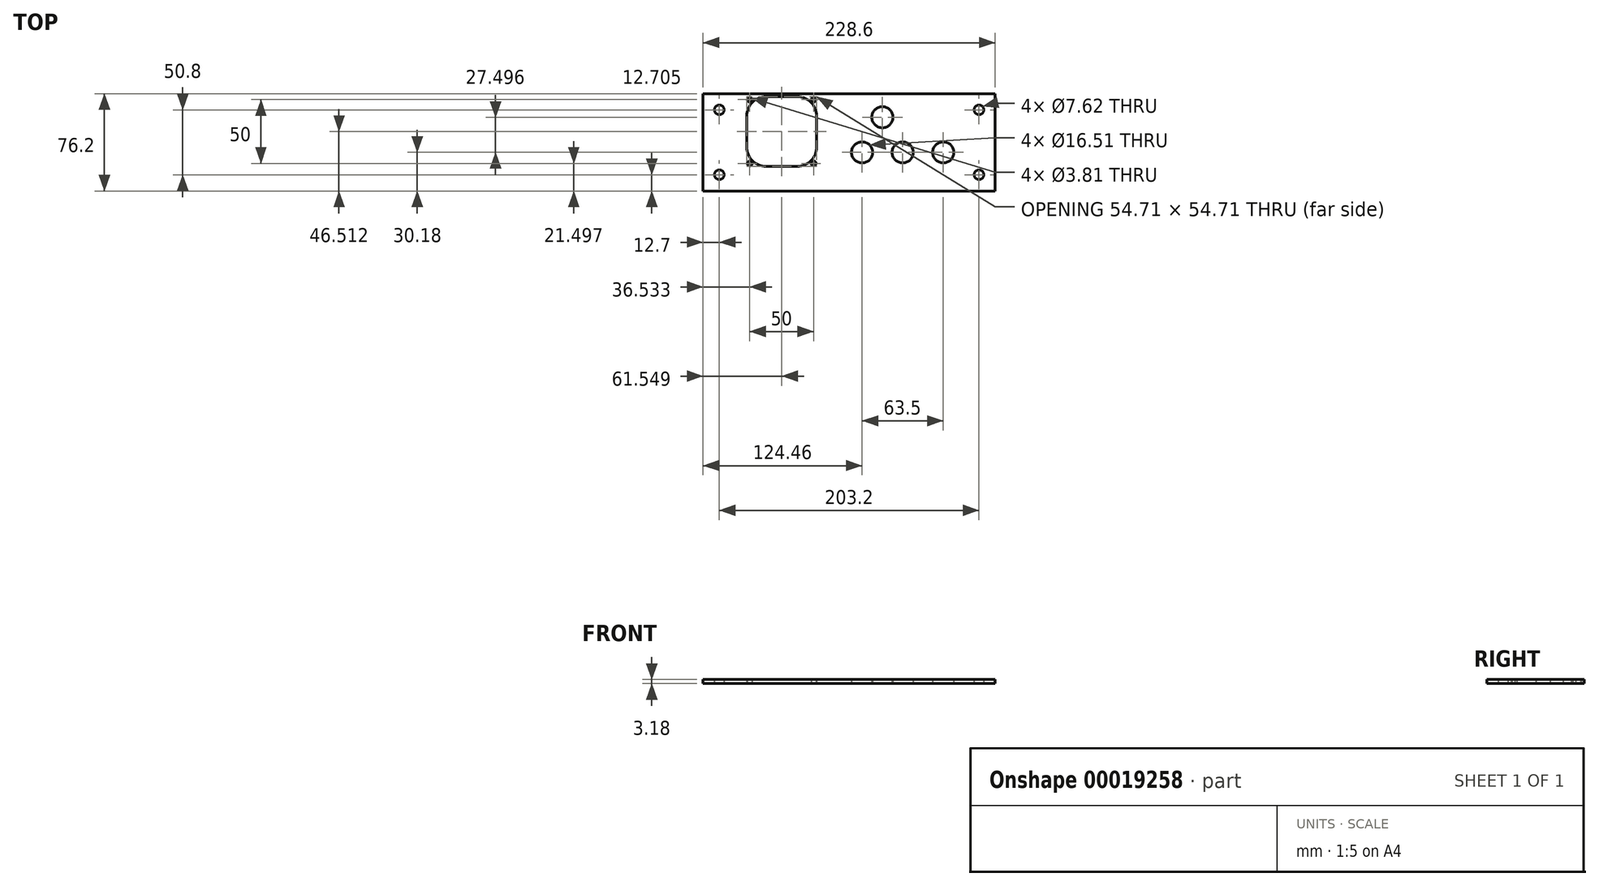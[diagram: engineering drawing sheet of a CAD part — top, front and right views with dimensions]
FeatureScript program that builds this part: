
annotation { "Feature Type Name" : "Feature", "Feature Type Description" : "" }
export const myFeature = defineFeature(function(context is Context, id is Id, definition is map)
    precondition{}
    {
        {
            var Q0;
            Q0=qCreatedBy(makeId("Top.planeOp"),FACE);
            var sketch = newSketch(context, id + "F0", { "sketchPlane" : qUnion([Q0])});
            skLineSegment(sketch, "E0.bottom", {"start": v(-121.64, 45.12) * mm, "end": v(106.96, 45.12) * mm});
            skLineSegment(sketch, "E0.top", {"start": v(-121.64, -31.08) * mm, "end": v(106.96, -31.08) * mm});
            skLineSegment(sketch, "E0.left", {"start": v(-121.64, 45.12) * mm, "end": v(-121.64, -31.08) * mm});
            skLineSegment(sketch, "E0.right", {"start": v(106.96, 45.12) * mm, "end": v(106.96, -31.08) * mm});
            skLineSegment(sketch, "E1", {"start": v(-96.24, 45.12) * mm, "end": v(-96.24, -31.08) * mm, "construction": true});
            skLineSegment(sketch, "E2", {"start": v(81.56, 45.12) * mm, "end": v(81.56, -31.08) * mm, "construction": true});
            skLineSegment(sketch, "E3", {"start": v(-121.64, 19.72) * mm, "end": v(-96.24, 19.72) * mm, "construction": true});
            skLineSegment(sketch, "E4", {"start": v(-121.64, -5.68) * mm, "end": v(-96.24, -5.68) * mm, "construction": true});
            skLineSegment(sketch, "E5", {"start": v(81.56, 19.72) * mm, "end": v(106.96, 19.72) * mm, "construction": true});
            skLineSegment(sketch, "E6", {"start": v(81.56, -5.68) * mm, "end": v(106.96, -5.68) * mm, "construction": true});
            skLineSegment(sketch, "E7", {"start": v(-96.24, 45.12) * mm, "end": v(-121.64, 19.72) * mm, "construction": true});
            skLineSegment(sketch, "E8", {"start": v(81.56, 45.12) * mm, "end": v(106.96, 19.72) * mm, "construction": true});
            skLineSegment(sketch, "E9", {"start": v(81.56, -31.08) * mm, "end": v(106.96, -5.68) * mm, "construction": true});
            skLineSegment(sketch, "E10", {"start": v(-96.24, -31.08) * mm, "end": v(-121.64, -5.68) * mm, "construction": true});
            skCircle(sketch, "E11", {"center": v(-108.94, 32.42) * mm, "radius": 3.81 * mm});
            skCircle(sketch, "E12", {"center": v(-108.94, -18.38) * mm, "radius": 3.81 * mm});
            skCircle(sketch, "E13", {"center": v(94.26, 32.42) * mm, "radius": 3.81 * mm});
            skCircle(sketch, "E14", {"center": v(94.26, -18.38) * mm, "radius": 3.81 * mm});
            skCircle(sketch, "E15", {"center": v(66.32, -0.9) * mm, "radius": 8.26 * mm});
            skCircle(sketch, "E16", {"center": v(34.57, -0.9) * mm, "radius": 8.26 * mm});
            skCircle(sketch, "E17", {"center": v(2.82, -0.9) * mm, "radius": 8.26 * mm});
            skLineSegment(sketch, "E18.bottom", {"start": v(-72.2, 42.79) * mm, "end": v(-47.98, 42.79) * mm});
            skLineSegment(sketch, "E18.top", {"start": v(-72.2, -11.92) * mm, "end": v(-47.98, -11.92) * mm});
            skLineSegment(sketch, "E18.left", {"start": v(-87.45, 27.55) * mm, "end": v(-87.45, 3.32) * mm});
            skLineSegment(sketch, "E18.right", {"start": v(-32.74, 27.55) * mm, "end": v(-32.74, 3.32) * mm});
            skPoint(sketch, "E19.visualSharp", {"position": v(-87.45, 42.79) * mm});
            skArc(sketch, "E19.filletArc", {"start": v(-72.2, 42.79) * mm, "mid": v(-82.98, 38.32) * mm, "end": v(-87.45, 27.55) * mm});
            skPoint(sketch, "E20.visualSharp", {"position": v(-32.74, 42.79) * mm});
            skArc(sketch, "E20.filletArc", {"start": v(-32.74, 27.55) * mm, "mid": v(-37.2, 38.32) * mm, "end": v(-47.98, 42.79) * mm});
            skPoint(sketch, "E21.visualSharp", {"position": v(-32.74, -11.92) * mm});
            skArc(sketch, "E21.filletArc", {"start": v(-47.98, -11.92) * mm, "mid": v(-37.2, -7.46) * mm, "end": v(-32.74, 3.32) * mm});
            skPoint(sketch, "E22.visualSharp", {"position": v(-87.45, -11.92) * mm});
            skArc(sketch, "E22.filletArc", {"start": v(-87.45, 3.32) * mm, "mid": v(-82.98, -7.46) * mm, "end": v(-72.2, -11.92) * mm});
            skLineSegment(sketch, "E23", {"start": v(-85.1, 40.42) * mm, "end": v(-85.1, -9.58) * mm, "construction": true});
            skLineSegment(sketch, "E24", {"start": v(-85.1, 40.42) * mm, "end": v(-35.1, 40.42) * mm, "construction": true});
            skLineSegment(sketch, "E25", {"start": v(-35.1, 40.42) * mm, "end": v(-35.1, -9.55) * mm, "construction": true});
            skLineSegment(sketch, "E26", {"start": v(-35.1, -9.55) * mm, "end": v(-85.1, -9.58) * mm, "construction": true});
            skCircle(sketch, "E27", {"center": v(-85.1, 40.42) * mm, "radius": 1.9 * mm});
            skCircle(sketch, "E28", {"center": v(-35.1, 40.42) * mm, "radius": 1.9 * mm});
            skCircle(sketch, "E29", {"center": v(-85.1, -9.58) * mm, "radius": 1.9 * mm});
            skCircle(sketch, "E30", {"center": v(-35.1, -9.55) * mm, "radius": 1.9 * mm});
            skCircle(sketch, "E31", {"center": v(18.7, 26.6) * mm, "radius": 8.26 * mm});
            skSolve(sketch);
        }
        {
            var Q0;
            {var subQ7=sQuery(id+"F0.wireOp",EDGE,"E6");Q0=makeQuery(id+"F0.imprint","IMPRINT",FACE,{"disambiguationData":[TD([[makeQuery(id+"F0.imprint","IMPRINT",EDGE,{"derivedFrom":subQ7}),-1.0]])]});}
            var Q1;
            {var subQ0=sQuery(id+"F0.wireOp",EDGE,"E13");var subQ3=sQuery(id+"F0.wireOp",EDGE,"E8");var subQ4=makeQuery(id+"F0.imprint","INTERSECT",VERTEX,{"disambiguationData":[OD(0.0)],"derivedFrom":[subQ3,subQ0]});Q1=makeQuery(id+"F0.imprint","IMPRINT",FACE,{"disambiguationData":[TD([[makeQuery(id+"F0.imprint","IMPRINT",EDGE,{"disambiguationData":[TD([[subQ4,-1.0]])],"derivedFrom":subQ0}),-1.0]])]});}
            var Q2;
            {var subQ0=sQuery(id+"F0.wireOp",EDGE,"E14");var subQ3=sQuery(id+"F0.wireOp",EDGE,"c62949cf-7a89-4347-aa41-fc8caa8e95c9");var subQ4=makeQuery(id+"F0.imprint","INTERSECT",VERTEX,{"disambiguationData":[OD(0.0)],"derivedFrom":[subQ3,subQ0]});Q2=makeQuery(id+"F0.imprint","IMPRINT",FACE,{"disambiguationData":[TD([[makeQuery(id+"F0.imprint","IMPRINT",EDGE,{"disambiguationData":[TD([[subQ4,-1.0]])],"derivedFrom":subQ0}),-1.0]])]});}
            var Q3;
            {var subQ8=sQuery(id+"F0.wireOp",EDGE,"E4");Q3=makeQuery(id+"F0.imprint","IMPRINT",FACE,{"disambiguationData":[TD([[makeQuery(id+"F0.imprint","IMPRINT",EDGE,{"derivedFrom":subQ8}),-1.0]])]});}
            var Q4;
            {var subQ0=sQuery(id+"F0.wireOp",EDGE,"2d4bd6bd-eb30-4121-a660-5daf919b16a9");var subQ3=sQuery(id+"F0.wireOp",EDGE,"E1");var subQ4=makeQuery(id+"F0.imprint","INTERSECT",VERTEX,{"derivedFrom":[subQ3,subQ0]});Q4=makeQuery(id+"F0.imprint","IMPRINT",FACE,{"disambiguationData":[TD([[makeQuery(id+"F0.imprint","IMPRINT",EDGE,{"disambiguationData":[TD([[subQ4,-1.0]])],"derivedFrom":subQ0}),-1.0]])]});}
            var Q5;
            {var subQ5=sQuery(id+"F0.wireOp",EDGE,"E5");Q5=makeQuery(id+"F0.imprint","IMPRINT",FACE,{"disambiguationData":[TD([[makeQuery(id+"F0.imprint","IMPRINT",EDGE,{"derivedFrom":subQ5}),1.0]])]});}
            var Q6;
            {var subQ0=sQuery(id+"F0.wireOp",EDGE,"2d4bd6bd-eb30-4121-a660-5daf919b16a9");var subQ3=sQuery(id+"F0.wireOp",EDGE,"E1");var subQ4=makeQuery(id+"F0.imprint","INTERSECT",VERTEX,{"derivedFrom":[subQ3,subQ0]});Q6=makeQuery(id+"F0.imprint","IMPRINT",FACE,{"disambiguationData":[TD([[makeQuery(id+"F0.imprint","IMPRINT",EDGE,{"disambiguationData":[TD([[subQ4,1.0]])],"derivedFrom":subQ0}),1.0]])]});}
            var Q7;
            {var subQ0=sQuery(id+"F0.wireOp",EDGE,"2d4bd6bd-eb30-4121-a660-5daf919b16a9");var subQ3=sQuery(id+"F0.wireOp",EDGE,"E2");var subQ4=makeQuery(id+"F0.imprint","INTERSECT",VERTEX,{"derivedFrom":[subQ3,subQ0]});Q7=makeQuery(id+"F0.imprint","IMPRINT",FACE,{"disambiguationData":[TD([[makeQuery(id+"F0.imprint","IMPRINT",EDGE,{"disambiguationData":[TD([[subQ4,-1.0]])],"derivedFrom":subQ0}),1.0]])]});}
            var Q8;
            {var subQ0=sQuery(id+"F0.wireOp",EDGE,"E13");var subQ3=sQuery(id+"F0.wireOp",EDGE,"E8");var subQ4=makeQuery(id+"F0.imprint","INTERSECT",VERTEX,{"disambiguationData":[OD(0.0)],"derivedFrom":[subQ3,subQ0]});Q8=makeQuery(id+"F0.imprint","IMPRINT",FACE,{"disambiguationData":[TD([[makeQuery(id+"F0.imprint","IMPRINT",EDGE,{"disambiguationData":[TD([[subQ4,1.0]])],"derivedFrom":subQ0}),-1.0]])]});}
            var Q9;
            {var subQ0=sQuery(id+"F0.wireOp",EDGE,"E11");var subQ3=sQuery(id+"F0.wireOp",EDGE,"24e872d2-c15f-4dd6-86e6-8e7368f92cc2");var subQ4=makeQuery(id+"F0.imprint","INTERSECT",VERTEX,{"disambiguationData":[OD(0.0)],"derivedFrom":[subQ3,subQ0]});Q9=makeQuery(id+"F0.imprint","IMPRINT",FACE,{"disambiguationData":[TD([[makeQuery(id+"F0.imprint","IMPRINT",EDGE,{"disambiguationData":[TD([[subQ4,-1.0]])],"derivedFrom":subQ0}),-1.0]])]});}
            var Q10;
            {var subQ1=sQuery(id+"F0.wireOp",EDGE,"c62949cf-7a89-4347-aa41-fc8caa8e95c9");var subQ5=sQuery(id+"F0.wireOp",EDGE,"E14");var subQ8=makeQuery(id+"F0.imprint","INTERSECT",VERTEX,{"disambiguationData":[OD(1.0)],"derivedFrom":[subQ1,subQ5]});Q10=makeQuery(id+"F0.imprint","IMPRINT",FACE,{"disambiguationData":[TD([[makeQuery(id+"F0.imprint","IMPRINT",EDGE,{"disambiguationData":[TD([[subQ8,-1.0]])],"derivedFrom":subQ1}),1.0]])]});}
            var Q11;
            {var subQ0=sQuery(id+"F0.wireOp",EDGE,"E11");var subQ3=sQuery(id+"F0.wireOp",EDGE,"24e872d2-c15f-4dd6-86e6-8e7368f92cc2");var subQ4=makeQuery(id+"F0.imprint","INTERSECT",VERTEX,{"disambiguationData":[OD(1.0)],"derivedFrom":[subQ3,subQ0]});Q11=makeQuery(id+"F0.imprint","IMPRINT",FACE,{"disambiguationData":[TD([[makeQuery(id+"F0.imprint","IMPRINT",EDGE,{"disambiguationData":[TD([[subQ4,-1.0]])],"derivedFrom":subQ0}),-1.0]])]});}
            var Q12;
            {var subQ0=sQuery(id+"F0.wireOp",EDGE,"E11");var subQ3=sQuery(id+"F0.wireOp",EDGE,"24e872d2-c15f-4dd6-86e6-8e7368f92cc2");var subQ4=makeQuery(id+"F0.imprint","INTERSECT",VERTEX,{"disambiguationData":[OD(0.0)],"derivedFrom":[subQ3,subQ0]});Q12=makeQuery(id+"F0.imprint","IMPRINT",FACE,{"disambiguationData":[TD([[makeQuery(id+"F0.imprint","IMPRINT",EDGE,{"disambiguationData":[TD([[subQ4,1.0]])],"derivedFrom":subQ0}),-1.0]])]});}
            var Q13;
            {var subQ0=sQuery(id+"F0.wireOp",EDGE,"E12");var subQ3=sQuery(id+"F0.wireOp",EDGE,"E10");var subQ4=makeQuery(id+"F0.imprint","INTERSECT",VERTEX,{"disambiguationData":[OD(1.0)],"derivedFrom":[subQ3,subQ0]});Q13=makeQuery(id+"F0.imprint","IMPRINT",FACE,{"disambiguationData":[TD([[makeQuery(id+"F0.imprint","IMPRINT",EDGE,{"disambiguationData":[TD([[subQ4,-1.0]])],"derivedFrom":subQ0}),-1.0]])]});}
            var Q14;
            {var subQ1=sQuery(id+"F0.wireOp",EDGE,"E3");Q14=makeQuery(id+"F0.imprint","IMPRINT",FACE,{"disambiguationData":[TD([[makeQuery(id+"F0.imprint","IMPRINT",EDGE,{"derivedFrom":subQ1}),-1.0]])]});}
            var Q15;
            Q15=makeQuery(id+"F0.imprint","IMPRINT",FACE,{"disambiguationData":[TD([[makeQuery(id+"F0.imprint","IMPRINT",EDGE,{"derivedFrom":sQuery(id+"F0.wireOp",EDGE,"E15")}),-1.0]])]});
            var Q16;
            {var subQ0=sQuery(id+"F0.wireOp",EDGE,"E12");var subQ3=sQuery(id+"F0.wireOp",EDGE,"E10");var subQ4=makeQuery(id+"F0.imprint","INTERSECT",VERTEX,{"disambiguationData":[OD(0.0)],"derivedFrom":[subQ3,subQ0]});Q16=makeQuery(id+"F0.imprint","IMPRINT",FACE,{"disambiguationData":[TD([[makeQuery(id+"F0.imprint","IMPRINT",EDGE,{"disambiguationData":[TD([[subQ4,1.0]])],"derivedFrom":subQ0}),-1.0]])]});}
            var Q17;
            {var subQ5=sQuery(id+"F0.wireOp",EDGE,"E3");Q17=makeQuery(id+"F0.imprint","IMPRINT",FACE,{"disambiguationData":[TD([[makeQuery(id+"F0.imprint","IMPRINT",EDGE,{"derivedFrom":subQ5}),1.0]])]});}
            var Q18;
            {var subQ1=sQuery(id+"F0.wireOp",EDGE,"E5");Q18=makeQuery(id+"F0.imprint","IMPRINT",FACE,{"disambiguationData":[TD([[makeQuery(id+"F0.imprint","IMPRINT",EDGE,{"derivedFrom":subQ1}),-1.0]])]});}
            var Q19;
            {var subQ0=sQuery(id+"F0.wireOp",EDGE,"E13");var subQ3=sQuery(id+"F0.wireOp",EDGE,"E8");var subQ4=makeQuery(id+"F0.imprint","INTERSECT",VERTEX,{"disambiguationData":[OD(1.0)],"derivedFrom":[subQ3,subQ0]});Q19=makeQuery(id+"F0.imprint","IMPRINT",FACE,{"disambiguationData":[TD([[makeQuery(id+"F0.imprint","IMPRINT",EDGE,{"disambiguationData":[TD([[subQ4,-1.0]])],"derivedFrom":subQ0}),-1.0]])]});}
            var Q20;
            {var subQ1=sQuery(id+"F0.wireOp",EDGE,"c8b01d91-180b-4811-89f7-2dacd4489a70");var subQ5=sQuery(id+"F0.wireOp",EDGE,"E12");var subQ6=makeQuery(id+"F0.imprint","INTERSECT",VERTEX,{"disambiguationData":[OD(1.0)],"derivedFrom":[subQ1,subQ5]});Q20=makeQuery(id+"F0.imprint","IMPRINT",FACE,{"disambiguationData":[TD([[makeQuery(id+"F0.imprint","IMPRINT",EDGE,{"disambiguationData":[TD([[subQ6,-1.0]])],"derivedFrom":subQ1}),-1.0]])]});}
            var Q21;
            {var subQ0=sQuery(id+"F0.wireOp",EDGE,"E14");var subQ3=sQuery(id+"F0.wireOp",EDGE,"c62949cf-7a89-4347-aa41-fc8caa8e95c9");var subQ4=makeQuery(id+"F0.imprint","INTERSECT",VERTEX,{"disambiguationData":[OD(0.0)],"derivedFrom":[subQ3,subQ0]});Q21=makeQuery(id+"F0.imprint","IMPRINT",FACE,{"disambiguationData":[TD([[makeQuery(id+"F0.imprint","IMPRINT",EDGE,{"disambiguationData":[TD([[subQ4,1.0]])],"derivedFrom":subQ0}),-1.0]])]});}
            var Q22;
            {var subQ1=sQuery(id+"F0.wireOp",EDGE,"E12");var subQ3=sQuery(id+"F0.wireOp",EDGE,"c8b01d91-180b-4811-89f7-2dacd4489a70");var subQ5=makeQuery(id+"F0.imprint","INTERSECT",VERTEX,{"disambiguationData":[OD(1.0)],"derivedFrom":[subQ3,subQ1]});Q22=makeQuery(id+"F0.imprint","IMPRINT",FACE,{"disambiguationData":[TD([[makeQuery(id+"F0.imprint","IMPRINT",EDGE,{"disambiguationData":[TD([[subQ5,-1.0]])],"derivedFrom":subQ3}),1.0]])]});}
            var Q23;
            {var subQ3=sQuery(id+"F0.wireOp",EDGE,"26066580-d837-4928-a678-ef0d1039c56a");var subQ5=sQuery(id+"F0.wireOp",EDGE,"E19.filletArc");var subQ7=makeQuery(id+"F0.imprint","INTERSECT",VERTEX,{"derivedFrom":[subQ5,subQ3]});Q23=makeQuery(id+"F0.imprint","IMPRINT",FACE,{"disambiguationData":[TD([[makeQuery(id+"F0.imprint","IMPRINT",EDGE,{"disambiguationData":[TD([[subQ7,-1.0]])],"derivedFrom":subQ5}),-1.0]])]});}
            var Q24;
            {var subQ3=sQuery(id+"F0.wireOp",EDGE,"c8be99c8-36e3-41cc-a8f7-0d507e28c46f");var subQ5=sQuery(id+"F0.wireOp",EDGE,"E20.filletArc");var subQ7=makeQuery(id+"F0.imprint","INTERSECT",VERTEX,{"derivedFrom":[subQ5,subQ3]});Q24=makeQuery(id+"F0.imprint","IMPRINT",FACE,{"disambiguationData":[TD([[makeQuery(id+"F0.imprint","IMPRINT",EDGE,{"disambiguationData":[TD([[subQ7,-1.0]])],"derivedFrom":subQ5}),-1.0]])]});}
            var Q25;
            {var subQ3=sQuery(id+"F0.wireOp",EDGE,"26066580-d837-4928-a678-ef0d1039c56a");var subQ5=sQuery(id+"F0.wireOp",EDGE,"E21.filletArc");var subQ7=makeQuery(id+"F0.imprint","INTERSECT",VERTEX,{"derivedFrom":[subQ5,subQ3]});Q25=makeQuery(id+"F0.imprint","IMPRINT",FACE,{"disambiguationData":[TD([[makeQuery(id+"F0.imprint","IMPRINT",EDGE,{"disambiguationData":[TD([[subQ7,-1.0]])],"derivedFrom":subQ5}),-1.0]])]});}
            var Q26;
            {var subQ1=sQuery(id+"F0.wireOp",EDGE,"c62949cf-7a89-4347-aa41-fc8caa8e95c9");var subQ3=sQuery(id+"F0.wireOp",EDGE,"E14");var subQ5=makeQuery(id+"F0.imprint","INTERSECT",VERTEX,{"disambiguationData":[OD(1.0)],"derivedFrom":[subQ1,subQ3]});Q26=makeQuery(id+"F0.imprint","IMPRINT",FACE,{"disambiguationData":[TD([[makeQuery(id+"F0.imprint","IMPRINT",EDGE,{"disambiguationData":[TD([[subQ5,-1.0]])],"derivedFrom":subQ1}),-1.0]])]});}
            var Q27;
            {var subQ0=sQuery(id+"F0.wireOp",EDGE,"E23");var subQ3=sQuery(id+"F0.wireOp",EDGE,"E22.filletArc");var subQ4=makeQuery(id+"F0.imprint","INTERSECT",VERTEX,{"derivedFrom":[subQ3,subQ0]});Q27=makeQuery(id+"F0.imprint","IMPRINT",FACE,{"disambiguationData":[TD([[makeQuery(id+"F0.imprint","IMPRINT",EDGE,{"disambiguationData":[TD([[subQ4,-1.0]])],"derivedFrom":subQ3}),-1.0]])]});}
            var Q28;
            {var subQ1=sQuery(id+"F0.wireOp",EDGE,"E24");var subQ5=sQuery(id+"F0.wireOp",EDGE,"E19.filletArc");var subQ6=makeQuery(id+"F0.imprint","INTERSECT",VERTEX,{"derivedFrom":[subQ5,subQ1]});Q28=makeQuery(id+"F0.imprint","IMPRINT",FACE,{"disambiguationData":[TD([[makeQuery(id+"F0.imprint","IMPRINT",EDGE,{"disambiguationData":[TD([[subQ6,-1.0]])],"derivedFrom":subQ5}),-1.0]])]});}
            var Q29;
            {var subQ1=sQuery(id+"F0.wireOp",EDGE,"E25");var subQ5=sQuery(id+"F0.wireOp",EDGE,"E20.filletArc");var subQ6=makeQuery(id+"F0.imprint","INTERSECT",VERTEX,{"derivedFrom":[subQ5,subQ1]});Q29=makeQuery(id+"F0.imprint","IMPRINT",FACE,{"disambiguationData":[TD([[makeQuery(id+"F0.imprint","IMPRINT",EDGE,{"disambiguationData":[TD([[subQ6,-1.0]])],"derivedFrom":subQ5}),-1.0]])]});}
            var Q30;
            {var subQ3=sQuery(id+"F0.wireOp",EDGE,"E22.filletArc");var subQ5=sQuery(id+"F0.wireOp",EDGE,"c8be99c8-36e3-41cc-a8f7-0d507e28c46f");var subQ7=makeQuery(id+"F0.imprint","INTERSECT",VERTEX,{"derivedFrom":[subQ3,subQ5]});Q30=makeQuery(id+"F0.imprint","IMPRINT",FACE,{"disambiguationData":[TD([[makeQuery(id+"F0.imprint","IMPRINT",EDGE,{"disambiguationData":[TD([[subQ7,-1.0]])],"derivedFrom":subQ3}),-1.0]])]});}
            var Q31;
            {var subQ1=sQuery(id+"F0.wireOp",EDGE,"E26");var subQ5=sQuery(id+"F0.wireOp",EDGE,"E21.filletArc");var subQ6=makeQuery(id+"F0.imprint","INTERSECT",VERTEX,{"derivedFrom":[subQ5,subQ1]});Q31=makeQuery(id+"F0.imprint","IMPRINT",FACE,{"disambiguationData":[TD([[makeQuery(id+"F0.imprint","IMPRINT",EDGE,{"disambiguationData":[TD([[subQ6,-1.0]])],"derivedFrom":subQ5}),-1.0]])]});}
            var Q32;
            {var subQ1=sQuery(id+"F0.wireOp",EDGE,"E12");var subQ5=sQuery(id+"F0.wireOp",EDGE,"E10");var subQ6=makeQuery(id+"F0.imprint","INTERSECT",VERTEX,{"disambiguationData":[OD(0.0)],"derivedFrom":[subQ5,subQ1]});Q32=makeQuery(id+"F0.imprint","IMPRINT",FACE,{"disambiguationData":[TD([[makeQuery(id+"F0.imprint","IMPRINT",EDGE,{"disambiguationData":[TD([[subQ6,-1.0]])],"derivedFrom":subQ1}),-1.0]])]});}
            extrude(context, id + "F1", {"entities" : qUnion([Q0, Q1, Q2, Q3, Q4, Q5, Q6, Q7, Q8, Q9, Q10, Q11, Q12, Q13, Q14, Q15, Q16, Q17, Q18, Q19, Q20, Q21, Q22, Q23, Q24, Q25, Q26, Q27, Q28, Q29, Q30, Q31, Q32]), "depth" : 3.17 * mm});
        }
    });
